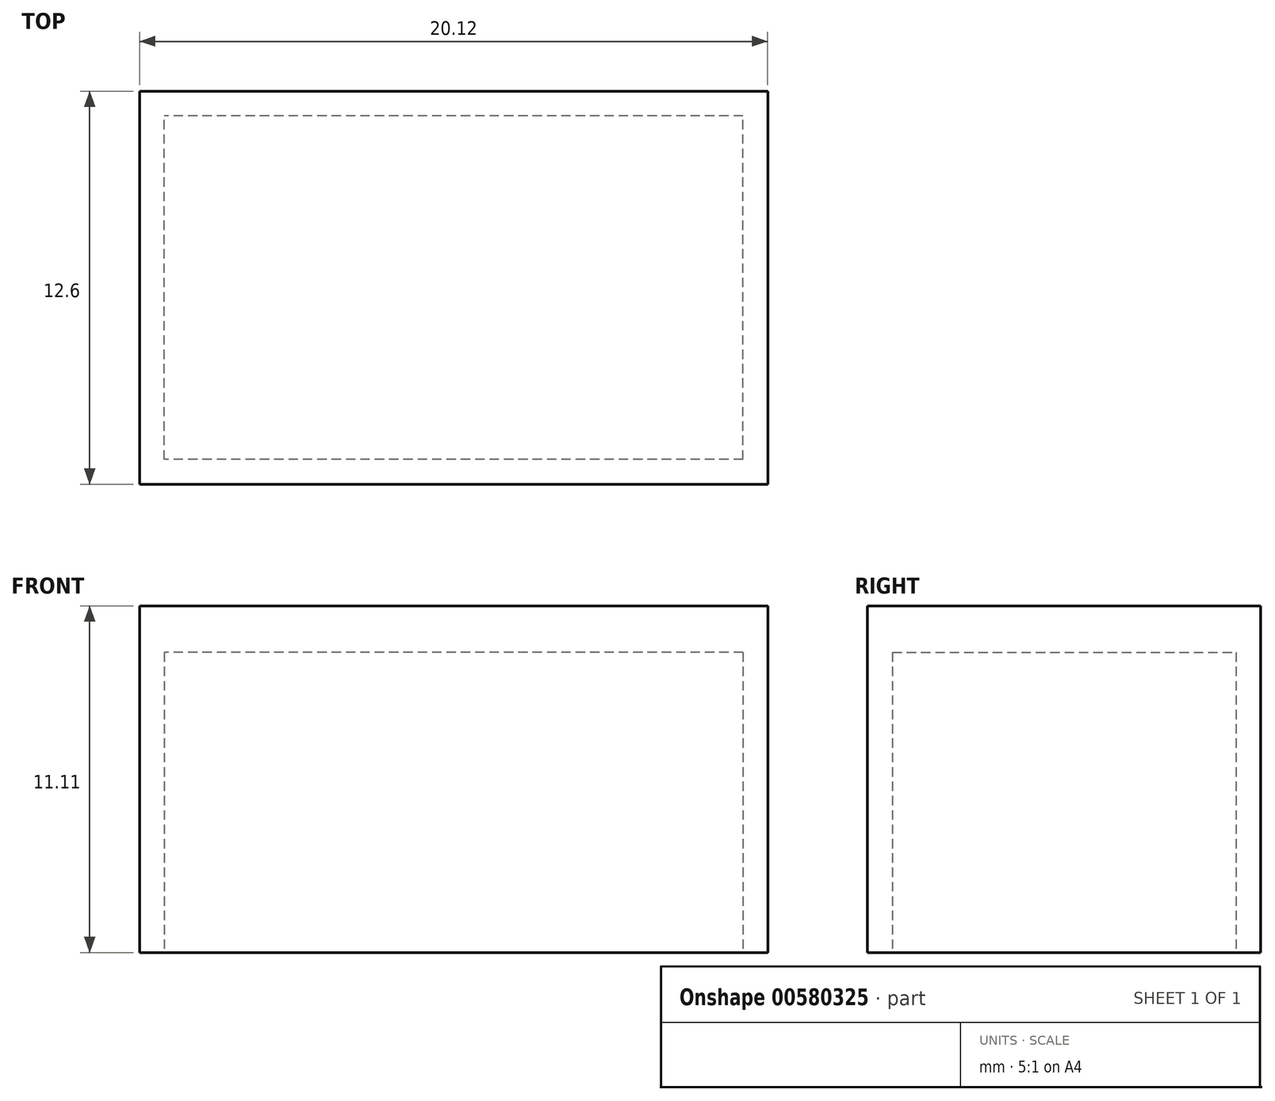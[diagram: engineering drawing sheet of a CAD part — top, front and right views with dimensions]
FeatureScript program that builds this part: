
annotation { "Feature Type Name" : "Feature", "Feature Type Description" : "" }
export const myFeature = defineFeature(function(context is Context, id is Id, definition is map)
    precondition{}
    {
        {
            var Q0;
            Q0=qCreatedBy(makeId("Top.planeOp"),FACE);
            var sketch = newSketch(context, id + "F0", { "sketchPlane" : qUnion([Q0])});
            skLineSegment(sketch, "E0.bottom", {"start": v(-10.06, -6.3) * mm, "end": v(10.07, -6.3) * mm});
            skLineSegment(sketch, "E0.top", {"start": v(-10.07, 6.3) * mm, "end": v(10.06, 6.3) * mm});
            skLineSegment(sketch, "E0.left", {"start": v(-10.06, -6.3) * mm, "end": v(-10.07, 6.3) * mm});
            skLineSegment(sketch, "E0.right", {"start": v(10.07, -6.3) * mm, "end": v(10.06, 6.3) * mm});
            skPoint(sketch, "E0.middle", {"position": v(0, 0) * mm});
            skSolve(sketch);
        }
        {
            var Q0;
            Q0 = qSketchRegion(id + "F0", true);
            extrude(context, id + "F1", {"entities" : qUnion([Q0]), "oppositeDirection" : true, "depth" : 11.1 * mm, "offsetDistance" : 25.4 * mm});
        }
        {
            var Q0;
            Q0=makeQuery(id+"F1.opExtrude","CAP_FACE",FACE,{"disambiguationData":[OSD([sQuery(id+"F0.wireOp",EDGE,"E0.bottom"),sQuery(id+"F0.wireOp",EDGE,"E0.top"),sQuery(id+"F0.wireOp",EDGE,"E0.left"),sQuery(id+"F0.wireOp",EDGE,"E0.right")])],"isStart":false});
            var sketch = newSketch(context, id + "F2", { "sketchPlane" : qUnion([Q0])});
            skLineSegment(sketch, "E1.bottom", {"start": v(9.27, 5.5) * mm, "end": v(-9.27, 5.5) * mm});
            skLineSegment(sketch, "E1.top", {"start": v(9.27, -5.5) * mm, "end": v(-9.27, -5.5) * mm});
            skLineSegment(sketch, "E1.left", {"start": v(9.27, 5.5) * mm, "end": v(9.27, -5.5) * mm});
            skLineSegment(sketch, "E1.right", {"start": v(-9.27, 5.5) * mm, "end": v(-9.27, -5.5) * mm});
            skPoint(sketch, "E1.middle", {"position": v(0, 0) * mm});
            skSolve(sketch);
        }
        {
            var Q0;
            Q0 = qSketchRegion(id + "F2", true);
            extrude(context, id + "F3", {"entities" : qUnion([Q0]), "operationType" : NewBodyOperationType.REMOVE, "oppositeDirection" : true, "depth" : 9.62 * mm, "offsetDistance" : 25.4 * mm});
        }
    });
